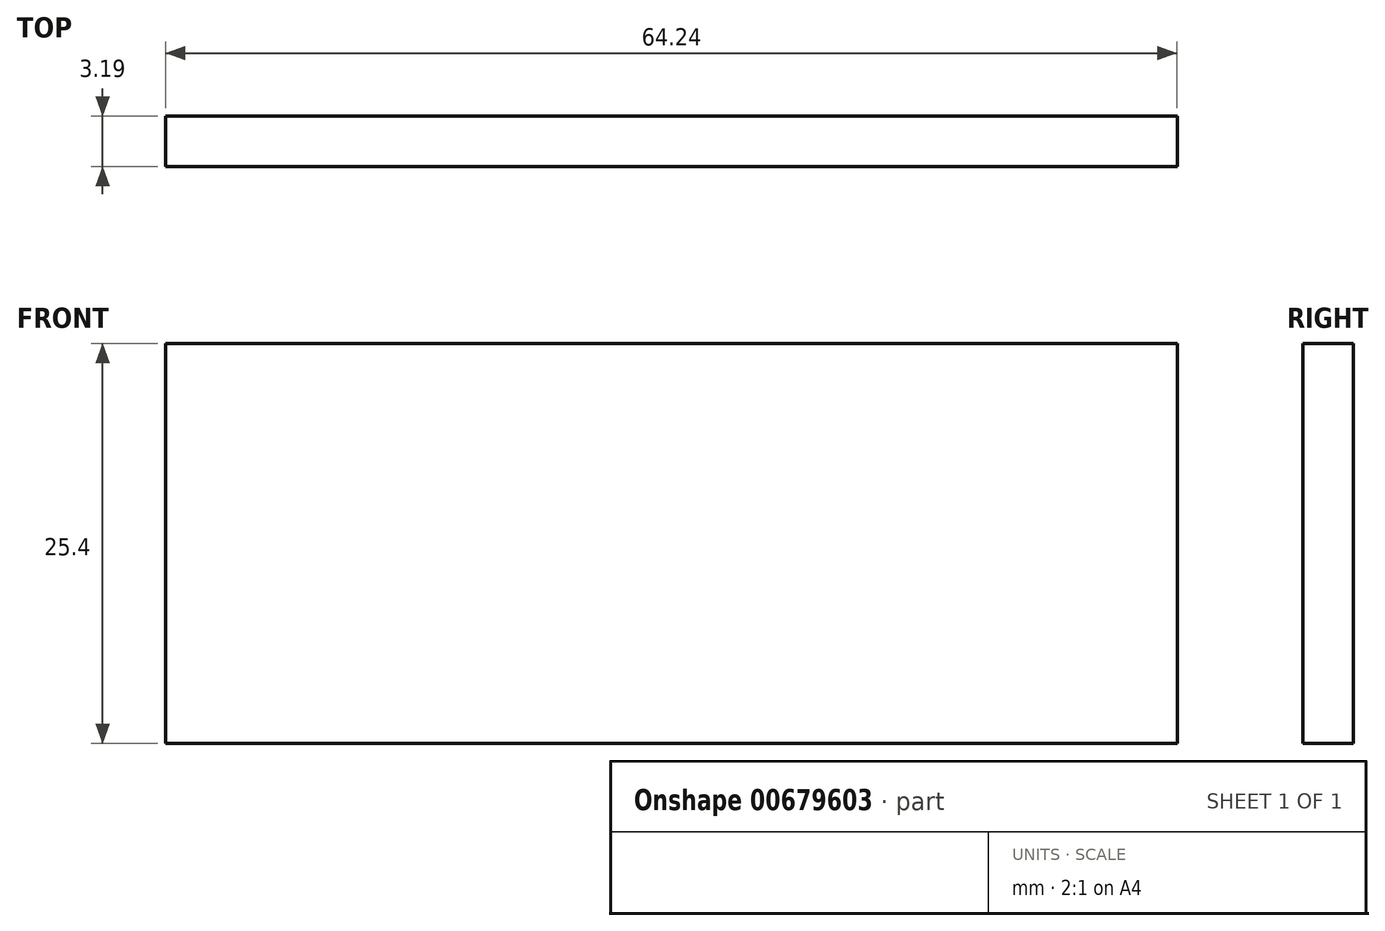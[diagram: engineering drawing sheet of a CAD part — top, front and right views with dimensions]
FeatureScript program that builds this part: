
annotation { "Feature Type Name" : "Feature", "Feature Type Description" : "" }
export const myFeature = defineFeature(function(context is Context, id is Id, definition is map)
    precondition{}
    {
        {
            var Q0;
            Q0=qCreatedBy(makeId("Top.planeOp"),FACE);
            var sketch = newSketch(context, id + "F0", { "sketchPlane" : qUnion([Q0])});
            skLineSegment(sketch, "E0.bottom", {"start": v(0, 0) * mm, "end": v(64.24, 0) * mm});
            skLineSegment(sketch, "E0.top", {"start": v(0, 3.19) * mm, "end": v(64.24, 3.19) * mm});
            skLineSegment(sketch, "E0.left", {"start": v(0, 0) * mm, "end": v(0, 3.19) * mm});
            skLineSegment(sketch, "E0.right", {"start": v(64.24, 0) * mm, "end": v(64.24, 3.19) * mm});
            skSolve(sketch);
        }
        {
            var Q0;
            Q0=makeQuery(id+"F0.imprint","IMPRINT",FACE,{"disambiguationData":[TD([[makeQuery(id+"F0.imprint","IMPRINT",EDGE,{"derivedFrom":sQuery(id+"F0.wireOp",EDGE,"E0.bottom")}),1.0]])]});
            extrude(context, id + "F1", {"entities" : qUnion([Q0]), "oppositeDirection" : true, "depth" : 25.4 * mm, "offsetDistance" : 25.4 * mm});
        }
    });
